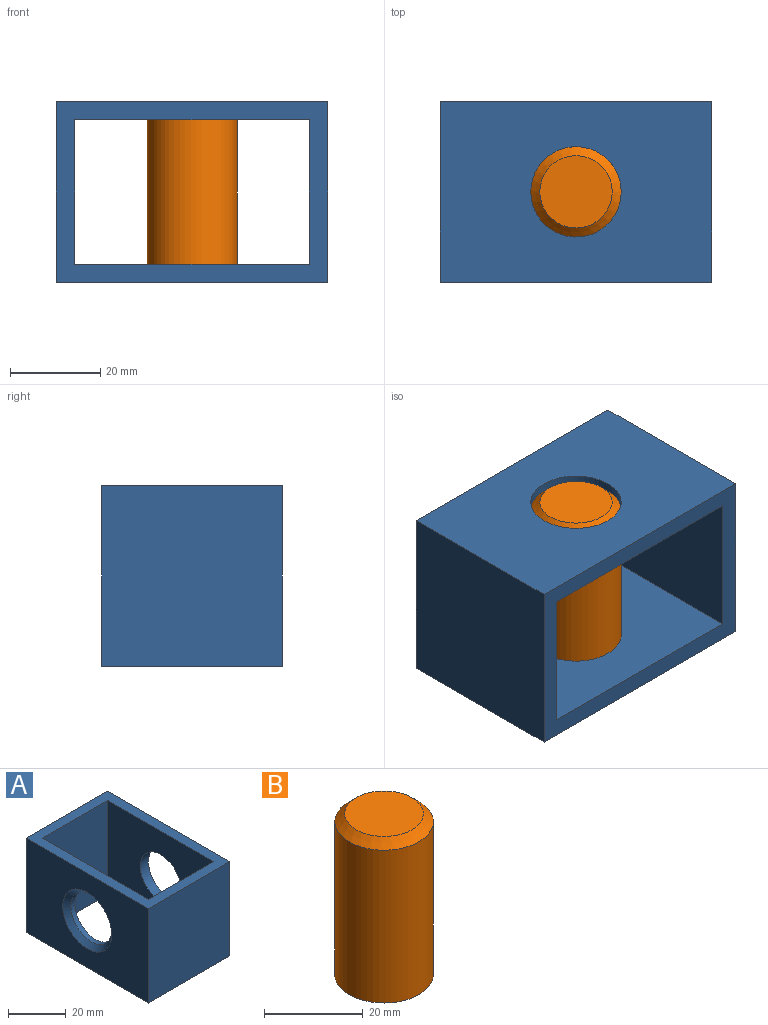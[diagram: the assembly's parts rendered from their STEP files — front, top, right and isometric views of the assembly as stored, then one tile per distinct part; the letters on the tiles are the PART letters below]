
ASSEMBLY  parts=2 mates=1
PART A: 13 faces, bbox 40x60x40 mm
  f0: plane 40x40mm, normal (0,-1,0), area 1600mm2, adj f1,f7,f8,f9
  f1: plane 60x40mm, normal (1,0,0), area 2085.8mm2, adj f0,f2,f8,f9,f11
  f2: plane 40x40mm, normal (0,1,0), area 1600mm2, adj f1,f7,f8,f9
  f3: plane 52x40mm, normal (-1,0,0), area 1765.8mm2, adj f4,f6,f8,f9,f11
  f4: plane 40x32mm, normal (0,1,0), area 1280mm2, adj f3,f5,f8,f9
  f5: plane 52x40mm, normal (1,0,0), area 1765.8mm2, adj f4,f6,f8,f9,f10
  f6: plane 40x32mm, normal (0,-1,0), area 1280mm2, adj f3,f5,f8,f9
  f7: plane 60x40mm, normal (-1,0,0), area 1947.6mm2, adj f0,f2,f8,f9,f12
  f8: plane 60x40mm, normal (0,0,1), area 736mm2, adj f0,f1,f2,f3,f4,f5,f6,f7
  f9: plane 60x40mm, normal (0,0,-1), area 736mm2, adj f0,f1,f2,f3,f4,f5,f6,f7
  f10: cylinder r=10mm len=20mm, axis (1,0,0), area 125.7mm2, adj f5,f12
  f11: cylinder r=10mm len=20mm, axis (1,0,0), area 251.3mm2, adj f1,f3
  f12: cone r=12mm half-angle=45deg, axis (-1,0,0), area 195.5mm2, adj f7,f10
PART B: 4 faces, bbox 20x20x40 mm
  f0: cylinder r=10mm len=38mm, axis (0,0,-1), area 2387.6mm2, adj f2,f3
  f1: plane 16x16mm, normal (0,0,1), area 201.1mm2, adj f3
  f2: plane 20x20mm, normal (0,0,-1), area 314.2mm2, adj f0
  f3: cone r=8mm half-angle=45deg, axis (0,0,-1), area 159.9mm2, adj f0,f1
PLACE A rot(axis=(-0.58,-0.58,-0.58),120deg) t=(31.86,-20,60.15)mm
PLACE B at identity
MATE fastened A.f10 <-> B.f0  axis (0,0,1) through (31.86,0,40)mm
